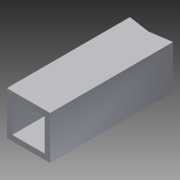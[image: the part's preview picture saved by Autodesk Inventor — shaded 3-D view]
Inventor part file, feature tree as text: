
AUTODESK INVENTOR PART (.ipt)
format: ipt  version: 2013 (Build 170138000, 138)  size: 89,600 bytes
history: native  units: in
note: dims shown in document units (in); Inventor stores cm internally (conversion verified against a paired STEP export)
features: extrude x2, sketch x2
ambient origin geometry x8: Origin, YZ Plane, XZ Plane, XY Plane, X Axis, Y Axis, Z Axis, Center Point
bodies: Solid1 (feature_tree)
feature tree (4):
  extrude  "Extrusion1"  Depth=1.0in
  extrude  "Extrusion2"  Depth=2.85in TaperAngle=0.0deg
  sketch  "Sketch1"  dims[d2=1.0in d4=1.0in]
  sketch  "Sketch2"  dims[d5=0.125in d6=2.85in d7=0.0in d8=0.075in d9=0.075in d10=1.0in d11=0.0in]
